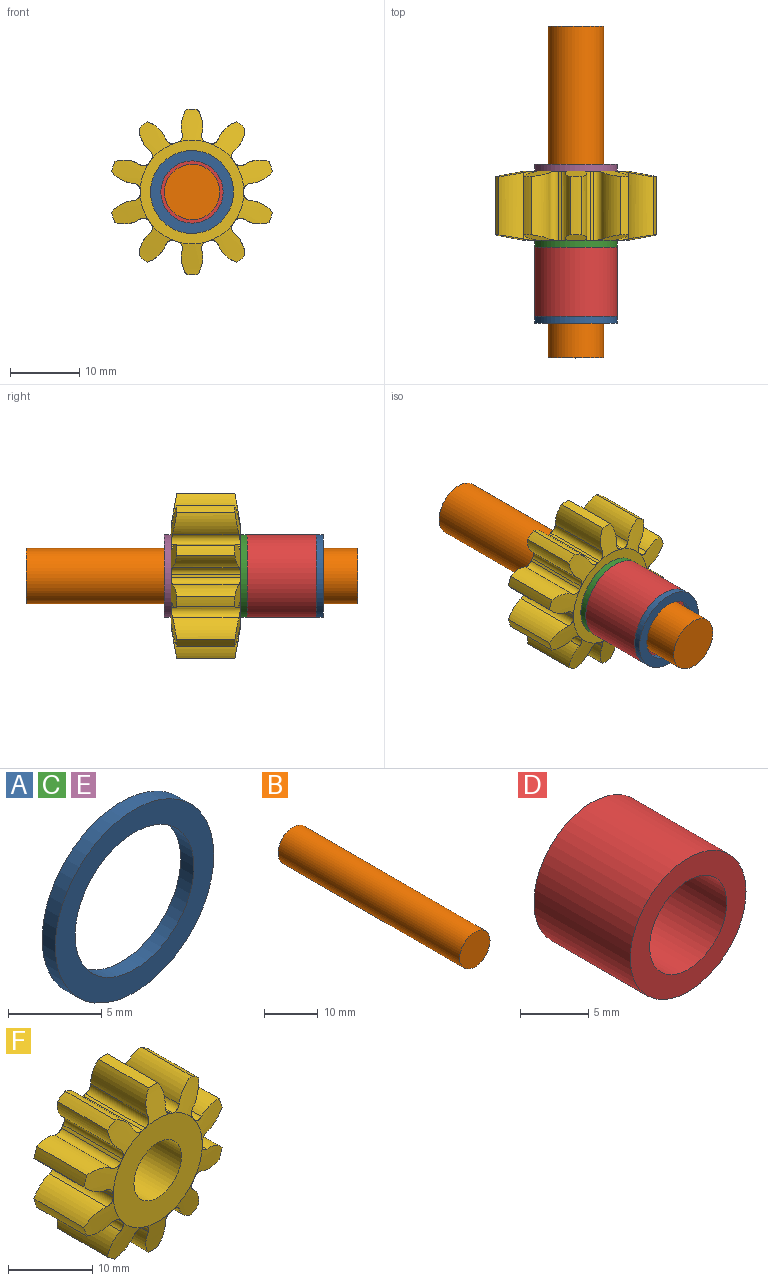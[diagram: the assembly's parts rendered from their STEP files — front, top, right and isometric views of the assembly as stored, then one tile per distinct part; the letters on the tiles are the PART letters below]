
ASSEMBLY  parts=6 mates=5
PART A: 4 faces, bbox 12x1x12 mm
  f0: cylinder r=4.5mm len=9mm, axis (0,1,0), area 28.3mm2, adj f2,f3
  f1: cylinder r=6mm len=12mm, axis (0,1,0), area 37.7mm2, adj f2,f3
  f2: plane 12x12mm, normal (0,-1,0), area 49.5mm2, adj f0,f1
  f3: plane 12x12mm, normal (0,1,0), area 49.5mm2, adj f0,f1
PART B: 3 faces, bbox 8x48x8 mm
  f0: cylinder r=4mm len=48mm, axis (0,1,0), area 1206.4mm2, adj f1,f2
  f1: plane 8x8mm, normal (0,-1,0), area 50.3mm2, adj f0
  f2: plane 8x8mm, normal (0,1,0), area 50.3mm2, adj f0
PART C: same geometry as A
PART D: 4 faces, bbox 12x10x12 mm
  f0: cylinder r=4mm len=10mm, axis (0,1,0), area 251.3mm2, adj f2,f3
  f1: cylinder r=6mm len=12mm, axis (0,1,0), area 377mm2, adj f2,f3
  f2: plane 12x12mm, normal (0,-1,0), area 62.8mm2, adj f0,f1
  f3: plane 12x12mm, normal (0,1,0), area 62.8mm2, adj f0,f1
PART E: same geometry as A
PART F: 83 faces, bbox 24x10x24 mm
  f0: plane 15x15mm, normal (0,-1,0), area 126.4mm2, adj f2,f3,f4,f5,f6,f7,f8,f9
  f1: plane 15x15mm, normal (0,1,0), area 126.4mm2, adj f2,f3,f4,f5,f6,f7,f8,f9
  f2: cylinder r=7.5mm len=10mm, axis (0,1,0), area 4.1mm2, adj f0,f1,f15,f61
  f3: cylinder r=7.5mm len=10mm, axis (0,1,0), area 4.1mm2, adj f0,f1,f56,f60
  f4: cylinder r=7.5mm len=10mm, axis (0,1,0), area 4.1mm2, adj f0,f1,f51,f55
  f5: cylinder r=7.5mm len=10mm, axis (0,1,0), area 4.1mm2, adj f0,f1,f46,f50
  f6: cylinder r=7.5mm len=10mm, axis (0,1,0), area 4.1mm2, adj f0,f1,f41,f45
  f7: cylinder r=7.5mm len=10mm, axis (0,1,0), area 4.1mm2, adj f0,f1,f36,f40
  f8: cylinder r=7.5mm len=10mm, axis (0,1,0), area 4.1mm2, adj f0,f1,f31,f35
  f9: cylinder r=7.5mm len=10mm, axis (0,1,0), area 4.1mm2, adj f0,f1,f26,f30
  f10: cylinder r=7.5mm len=10mm, axis (0,1,0), area 4.1mm2, adj f0,f1,f21,f25
  f11: cylinder r=7.5mm len=10mm, axis (0,1,0), area 4.1mm2, adj f0,f1,f16,f20
  f12: cylinder r=4.45mm len=9.64mm, axis (0,1,0), area 33.9mm2, adj f13,f16,f71,f81
  f13: cylinder r=12mm len=8.41mm, axis (0,1,0), area 13mm2, adj f12,f14,f71,f81
  f14: cylinder r=4.45mm len=9.64mm, axis (0,1,0), area 33.9mm2, adj f13,f15,f71,f81
  f15: cylinder r=1mm len=10mm, axis (0,1,0), area 15mm2, adj f2,f14,f71,f81
  f16: cylinder r=1mm len=10mm, axis (0,1,0), area 15mm2, adj f11,f12,f71,f81
  f17: cylinder r=4.45mm len=9.64mm, axis (0,1,0), area 33.9mm2, adj f18,f21,f70,f80
  f18: cylinder r=12mm len=8.41mm, axis (0,1,0), area 13mm2, adj f17,f19,f70,f80
  f19: cylinder r=4.45mm len=9.64mm, axis (0,1,0), area 33.9mm2, adj f18,f20,f70,f80
  f20: cylinder r=1mm len=10mm, axis (0,1,0), area 15mm2, adj f11,f19,f70,f80
  f21: cylinder r=1mm len=10mm, axis (0,1,0), area 15mm2, adj f10,f17,f70,f80
  f22: cylinder r=4.45mm len=9.64mm, axis (0,1,0), area 33.9mm2, adj f23,f26,f69,f79
  f23: cylinder r=12mm len=8.41mm, axis (0,1,0), area 13mm2, adj f22,f24,f69,f79
  f24: cylinder r=4.45mm len=9.64mm, axis (0,1,0), area 33.9mm2, adj f23,f25,f69,f79
  f25: cylinder r=1mm len=10mm, axis (0,1,0), area 15mm2, adj f10,f24,f69,f79
  f26: cylinder r=1mm len=10mm, axis (0,1,0), area 15mm2, adj f9,f22,f69,f79
  f27: cylinder r=4.45mm len=9.64mm, axis (0,1,0), area 33.9mm2, adj f28,f31,f68,f78
  f28: cylinder r=12mm len=8.41mm, axis (0,1,0), area 13mm2, adj f27,f29,f68,f78
  f29: cylinder r=4.45mm len=9.64mm, axis (0,1,0), area 33.9mm2, adj f28,f30,f68,f78
  f30: cylinder r=1mm len=10mm, axis (0,1,0), area 15mm2, adj f9,f29,f68,f78
  f31: cylinder r=1mm len=10mm, axis (0,1,0), area 15mm2, adj f8,f27,f68,f78
  f32: cylinder r=4.45mm len=9.64mm, axis (0,1,0), area 33.9mm2, adj f33,f36,f67,f77
  f33: cylinder r=12mm len=8.41mm, axis (0,1,0), area 13mm2, adj f32,f34,f67,f77
  f34: cylinder r=4.45mm len=9.64mm, axis (0,1,0), area 33.9mm2, adj f33,f35,f67,f77
  f35: cylinder r=1mm len=10mm, axis (0,1,0), area 15mm2, adj f8,f34,f67,f77
  f36: cylinder r=1mm len=10mm, axis (0,1,0), area 15mm2, adj f7,f32,f67,f77
  f37: cylinder r=4.45mm len=9.64mm, axis (0,1,0), area 33.9mm2, adj f38,f41,f66,f76
  f38: cylinder r=12mm len=8.41mm, axis (0,1,0), area 13mm2, adj f37,f39,f66,f76
  f39: cylinder r=4.45mm len=9.64mm, axis (0,1,0), area 33.9mm2, adj f38,f40,f66,f76
  f40: cylinder r=1mm len=10mm, axis (0,1,0), area 15mm2, adj f7,f39,f66,f76
  f41: cylinder r=1mm len=10mm, axis (0,1,0), area 15mm2, adj f6,f37,f66,f76
  f42: cylinder r=4.45mm len=9.64mm, axis (0,1,0), area 33.9mm2, adj f43,f46,f65,f75
  f43: cylinder r=12mm len=8.41mm, axis (0,1,0), area 13mm2, adj f42,f44,f65,f75
  f44: cylinder r=4.45mm len=9.64mm, axis (0,1,0), area 33.9mm2, adj f43,f45,f65,f75
  f45: cylinder r=1mm len=10mm, axis (0,1,0), area 15mm2, adj f6,f44,f65,f75
  f46: cylinder r=1mm len=10mm, axis (0,1,0), area 15mm2, adj f5,f42,f65,f75
  f47: cylinder r=4.45mm len=9.64mm, axis (0,1,0), area 33.9mm2, adj f48,f51,f64,f74
  f48: cylinder r=12mm len=8.41mm, axis (0,1,0), area 13mm2, adj f47,f49,f64,f74
  f49: cylinder r=4.45mm len=9.64mm, axis (0,1,0), area 33.9mm2, adj f48,f50,f64,f74
  f50: cylinder r=1mm len=10mm, axis (0,1,0), area 15mm2, adj f5,f49,f64,f74
  f51: cylinder r=1mm len=10mm, axis (0,1,0), area 15mm2, adj f4,f47,f64,f74
  f52: cylinder r=4.45mm len=9.64mm, axis (0,1,0), area 33.9mm2, adj f53,f56,f63,f73
  f53: cylinder r=12mm len=8.41mm, axis (0,1,0), area 13mm2, adj f52,f54,f63,f73
  f54: cylinder r=4.45mm len=9.64mm, axis (0,1,0), area 33.9mm2, adj f53,f55,f63,f73
  f55: cylinder r=1mm len=10mm, axis (0,1,0), area 15mm2, adj f4,f54,f63,f73
  f56: cylinder r=1mm len=10mm, axis (0,1,0), area 15mm2, adj f3,f52,f63,f73
  f57: cylinder r=4.45mm len=9.64mm, axis (0,1,0), area 33.9mm2, adj f58,f61,f62,f72
  f58: cylinder r=12mm len=8.41mm, axis (0,1,0), area 13mm2, adj f57,f59,f62,f72
  f59: cylinder r=4.45mm len=9.64mm, axis (0,1,0), area 33.9mm2, adj f58,f60,f62,f72
  f60: cylinder r=1mm len=10mm, axis (0,1,0), area 15mm2, adj f3,f59,f62,f72
  f61: cylinder r=1mm len=10mm, axis (0,1,0), area 15mm2, adj f2,f57,f62,f72
  f62: cone r=12.12mm half-angle=80deg, axis (0,-1,0), area 12.9mm2, adj f1,f57,f58,f59,f60,f61
  f63: cone r=12.12mm half-angle=80deg, axis (0,-1,0), area 12.9mm2, adj f1,f52,f53,f54,f55,f56
  f64: cone r=12.12mm half-angle=80deg, axis (0,-1,0), area 12.9mm2, adj f1,f47,f48,f49,f50,f51
  f65: cone r=12.12mm half-angle=80deg, axis (0,-1,0), area 12.9mm2, adj f1,f42,f43,f44,f45,f46
  f66: cone r=12.12mm half-angle=80deg, axis (0,-1,0), area 12.9mm2, adj f1,f37,f38,f39,f40,f41
  f67: cone r=12.12mm half-angle=80deg, axis (0,-1,0), area 12.9mm2, adj f1,f32,f33,f34,f35,f36
  f68: cone r=12.12mm half-angle=80deg, axis (0,-1,0), area 12.9mm2, adj f1,f27,f28,f29,f30,f31
  f69: cone r=12.12mm half-angle=80deg, axis (0,-1,0), area 12.9mm2, adj f1,f22,f23,f24,f25,f26
  f70: cone r=12.12mm half-angle=80deg, axis (0,-1,0), area 12.9mm2, adj f1,f17,f18,f19,f20,f21
  f71: cone r=12.12mm half-angle=80deg, axis (0,-1,0), area 12.9mm2, adj f1,f12,f13,f14,f15,f16
  f72: cone r=12.12mm half-angle=80deg, axis (0,1,0), area 12.9mm2, adj f0,f57,f58,f59,f60,f61
  f73: cone r=12.12mm half-angle=80deg, axis (0,1,0), area 12.9mm2, adj f0,f52,f53,f54,f55,f56
  f74: cone r=12.12mm half-angle=80deg, axis (0,1,0), area 12.9mm2, adj f0,f47,f48,f49,f50,f51
  f75: cone r=12.12mm half-angle=80deg, axis (0,1,0), area 12.9mm2, adj f0,f42,f43,f44,f45,f46
  f76: cone r=12.12mm half-angle=80deg, axis (0,1,0), area 12.9mm2, adj f0,f37,f38,f39,f40,f41
  f77: cone r=12.12mm half-angle=80deg, axis (0,1,0), area 12.9mm2, adj f0,f32,f33,f34,f35,f36
  f78: cone r=12.12mm half-angle=80deg, axis (0,1,0), area 12.9mm2, adj f0,f27,f28,f29,f30,f31
  f79: cone r=12.12mm half-angle=80deg, axis (0,1,0), area 12.9mm2, adj f0,f22,f23,f24,f25,f26
  f80: cone r=12.12mm half-angle=80deg, axis (0,1,0), area 12.9mm2, adj f0,f17,f18,f19,f20,f21
  f81: cone r=12.12mm half-angle=80deg, axis (0,1,0), area 12.9mm2, adj f0,f12,f13,f14,f15,f16
  f82: cylinder r=4mm len=10mm, axis (0,-1,0), area 251.3mm2, adj f0,f1
PLACE A rot(axis=(1,0,0),180deg) t=(0,5,0)mm
PLACE B rot(axis=(-1,0,0),0deg) t=(0,48,0)mm
PLACE C t=(0,17,0)mm
PLACE D t=(0,11,0)mm
PLACE E t=(0,28,0)mm
PLACE F t=(0,22,0)mm
MATE fastened A.f0 <-> D.f0  axis (0,1,0) through (0,6,0)mm
MATE fastened C.f0 <-> F.f2  axis (0,1,0) through (0,17,0)mm
MATE fastened C.f0 <-> D.f0  axis (0,-1,0) through (0,16,0)mm
MATE fastened E.f0 <-> F.f2  axis (0,-1,0) through (0,27,0)mm
MATE fastened B.f0 <-> A.f0  axis (0,-1,0) through (0,0,0)mm
